# Revit family: Zumtobel AMBITUS
name_source: partatom
category: Lighting Fixtures
revit_build: Autodesk Revit 2018 (Build: 20170223_1515(x64)
units: mm (PartAtom-declared; Revit-internal decimal feet)

## family parameters
Cut with Voids When Loaded = No
Host = Face
Light Source = Yes
OmniClass Number = 23.80.70.11
OmniClass Title = Luminaries for Internal Lighting
Part Type = Normal
Room Calculation Point = No
Round Connector Dimension = Use Diameter
Shared = No

## types (1)
- AMBITUS DI 10k-930 MRC AST2 LDE SRE
    Apparent Load = 104 VA
    Assembly Code = D5020200
    Color Filter = 16777215
    Default Elevation = 0 mm  [stored 0 ft]
    Description = Circular LED luminaire
    Dimming Lamp Color Temperature Shift = <None>
    Emit Shape Visible in Rendering = Yes
    Emit from Circle Diameter = 442 mm  [stored 1.45013 ft]
    Height = 24 mm  [stored 0.0787402 ft]
    Lamp = LED
    Length = 600 mm
    Manufacturer = Zumtobel Lighting
    Model = 42189257
    Photometric Web File = 42189257_(STD_LEO).IES
    Radius = 300 mm  [stored 0.984252 ft]
    Tilt Angle = 90.00°
    URL = www.zumtobel.com/42189257
    Voltage = 230 V
    Width = 600 mm

note: [stored X ft] marks values corroborated as IEEE doubles in the binary element streams (Revit-internal decimal feet)

## geometry (parser evidence)
native form markers: Sweep x3
no freeform markers — native parametric forms only
